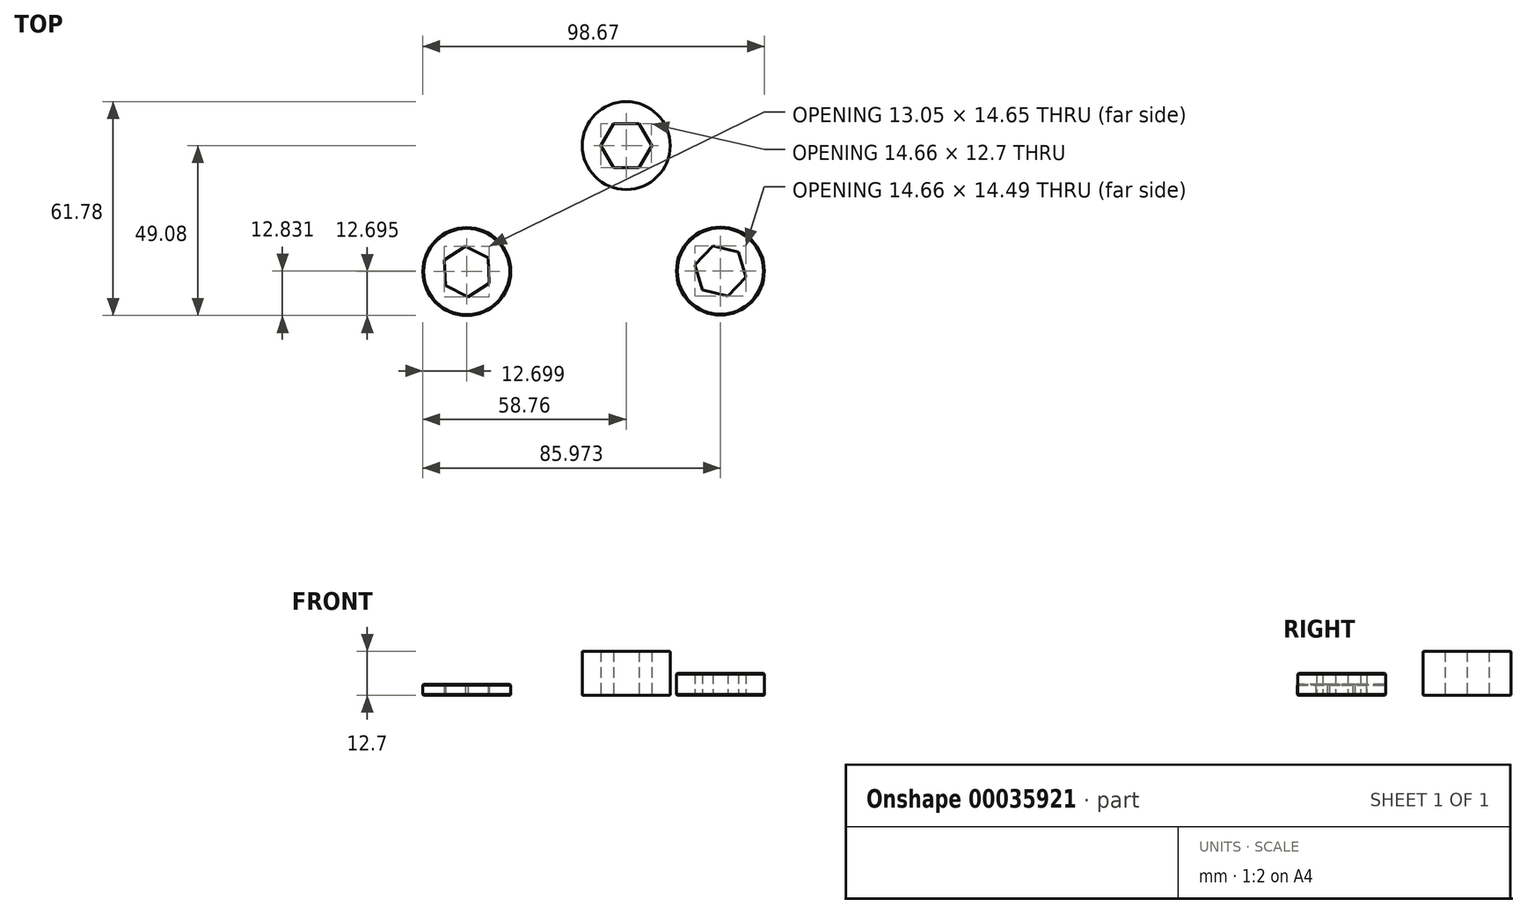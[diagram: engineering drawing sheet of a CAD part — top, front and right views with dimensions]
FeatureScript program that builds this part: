
annotation { "Feature Type Name" : "Feature", "Feature Type Description" : "" }
export const myFeature = defineFeature(function(context is Context, id is Id, definition is map)
    precondition{}
    {
        {
            var Q0;
            Q0=qCreatedBy(makeId("Top.planeOp"),FACE);
            var sketch = newSketch(context, id + "F0", { "sketchPlane" : qUnion([Q0])});
            skCircle(sketch, "E0.cCircle", {"center": v(0, 0) * mm, "radius": 6.35 * mm, "construction": true});
            skLineSegment(sketch, "E0.0", {"start": v(7.33, 0) * mm, "end": v(3.67, -6.35) * mm});
            skLineSegment(sketch, "E0.1", {"start": v(3.67, -6.35) * mm, "end": v(-3.66, -6.35) * mm});
            skLineSegment(sketch, "E0.2", {"start": v(-3.66, -6.35) * mm, "end": v(-7.33, 0) * mm});
            skLineSegment(sketch, "E0.3", {"start": v(-7.33, 0) * mm, "end": v(-3.67, 6.35) * mm});
            skLineSegment(sketch, "E0.4", {"start": v(-3.67, 6.35) * mm, "end": v(3.66, 6.35) * mm});
            skLineSegment(sketch, "E0.5", {"start": v(3.66, 6.35) * mm, "end": v(7.33, 0) * mm});
            skCircle(sketch, "E1", {"center": v(0, 0) * mm, "radius": 12.7 * mm});
            skSolve(sketch);
        }
        {
            var Q0;
            Q0=makeQuery(id+"F0.imprint","IMPRINT",FACE,{"disambiguationData":[TD([[makeQuery(id+"F0.imprint","IMPRINT",EDGE,{"derivedFrom":sQuery(id+"F0.wireOp",EDGE,"E0.0")}),1.0]])]});
            extrude(context, id + "F1", {"entities" : qUnion([Q0]), "depth" : 12.7 * mm});
        }
        {
            var Q0;
            Q0=makeQuery(id+"F1.opExtrude","CAP_EDGE",EDGE,{"disambiguationData":[OSD([sQuery(id+"F0.wireOp",EDGE,"E1")])],"isStart":false});
            var Q1;
            Q1=makeQuery(id+"F1.opExtrude","CAP_EDGE",EDGE,{"disambiguationData":[OSD([sQuery(id+"F0.wireOp",EDGE,"E1")])],"isStart":true});
            fillet(context, id + "F2", {"entities" : qUnion([Q0, Q1]), "radius" : 0.25 * mm, "tangentPropagation" : true, "allowEdgeOverflow" : false});
        }
        {
            var Q0;
            Q0=qCreatedBy(makeId("Top.planeOp"),FACE);
            var sketch = newSketch(context, id + "F3", { "sketchPlane" : qUnion([Q0])});
            skCircle(sketch, "E2", {"center": v(-46.06, -36.38) * mm, "radius": 12.7 * mm});
            skCircle(sketch, "E3.cCircle", {"center": v(-46.06, -36.38) * mm, "radius": 6.35 * mm, "construction": true});
            skLineSegment(sketch, "E3.0", {"start": v(-39.54, -39.73) * mm, "end": v(-45.7, -43.7) * mm});
            skLineSegment(sketch, "E3.1", {"start": v(-45.7, -43.7) * mm, "end": v(-52.22, -40.36) * mm});
            skLineSegment(sketch, "E3.2", {"start": v(-52.22, -40.36) * mm, "end": v(-52.58, -33.04) * mm});
            skLineSegment(sketch, "E3.3", {"start": v(-52.58, -33.04) * mm, "end": v(-46.42, -29.06) * mm});
            skLineSegment(sketch, "E3.4", {"start": v(-46.42, -29.06) * mm, "end": v(-39.9, -32.4) * mm});
            skLineSegment(sketch, "E3.5", {"start": v(-39.9, -32.4) * mm, "end": v(-39.54, -39.73) * mm});
            skPoint(sketch, "E3.0.midPoint", {"position": v(-42.62, -41.72) * mm});
            skSolve(sketch);
        }
        {
            var Q0;
            Q0 = qSketchRegion(id + "F3", true);
            extrude(context, id + "F4", {"entities" : qUnion([Q0]), "depth" : 3.17 * mm});
        }
        {
            var Q0;
            Q0=makeQuery(id+"F4.opExtrude","CAP_EDGE",EDGE,{"disambiguationData":[OSD([sQuery(id+"F3.wireOp",EDGE,"E2")])],"isStart":false});
            var Q1;
            Q1=makeQuery(id+"F4.opExtrude","CAP_EDGE",EDGE,{"disambiguationData":[OSD([sQuery(id+"F3.wireOp",EDGE,"E2")])],"isStart":true});
            chamfer(context, id + "F5", {"entities" : qUnion([Q0, Q1]), "width" : 0.25 * mm, "tangentPropagation" : true});
        }
        {
            var Q0;
            Q0=qCreatedBy(makeId("Top.planeOp"),FACE);
            var sketch = newSketch(context, id + "F6", { "sketchPlane" : qUnion([Q0])});
            skCircle(sketch, "E4", {"center": v(27.21, -36.25) * mm, "radius": 12.7 * mm});
            skCircle(sketch, "E5.cCircle", {"center": v(27.21, -36.25) * mm, "radius": 6.54 * mm, "construction": true});
            skLineSegment(sketch, "E5.0", {"start": v(34.54, -38.04) * mm, "end": v(29.33, -43.5) * mm});
            skLineSegment(sketch, "E5.1", {"start": v(29.33, -43.5) * mm, "end": v(22, -41.7) * mm});
            skLineSegment(sketch, "E5.2", {"start": v(22, -41.7) * mm, "end": v(19.88, -34.46) * mm});
            skLineSegment(sketch, "E5.3", {"start": v(19.88, -34.46) * mm, "end": v(25.1, -29) * mm});
            skLineSegment(sketch, "E5.4", {"start": v(25.1, -29) * mm, "end": v(32.43, -30.8) * mm});
            skLineSegment(sketch, "E5.5", {"start": v(32.43, -30.8) * mm, "end": v(34.54, -38.04) * mm});
            skPoint(sketch, "E5.0.midPoint", {"position": v(31.94, -40.77) * mm});
            skSolve(sketch);
        }
        {
            var Q0;
            Q0 = qSketchRegion(id + "F6", true);
            extrude(context, id + "F7", {"entities" : qUnion([Q0]), "depth" : 6.35 * mm});
        }
        {
            var Q0;
            Q0=makeQuery(id+"F7.opExtrude","CAP_EDGE",EDGE,{"disambiguationData":[OSD([sQuery(id+"F6.wireOp",EDGE,"E4")])],"isStart":false});
            var Q1;
            Q1=makeQuery(id+"F7.opExtrude","CAP_EDGE",EDGE,{"disambiguationData":[OSD([sQuery(id+"F6.wireOp",EDGE,"E4")])],"isStart":true});
            chamfer(context, id + "F8", {"entities" : qUnion([Q0, Q1]), "width" : 0.25 * mm, "tangentPropagation" : true});
        }
    });
